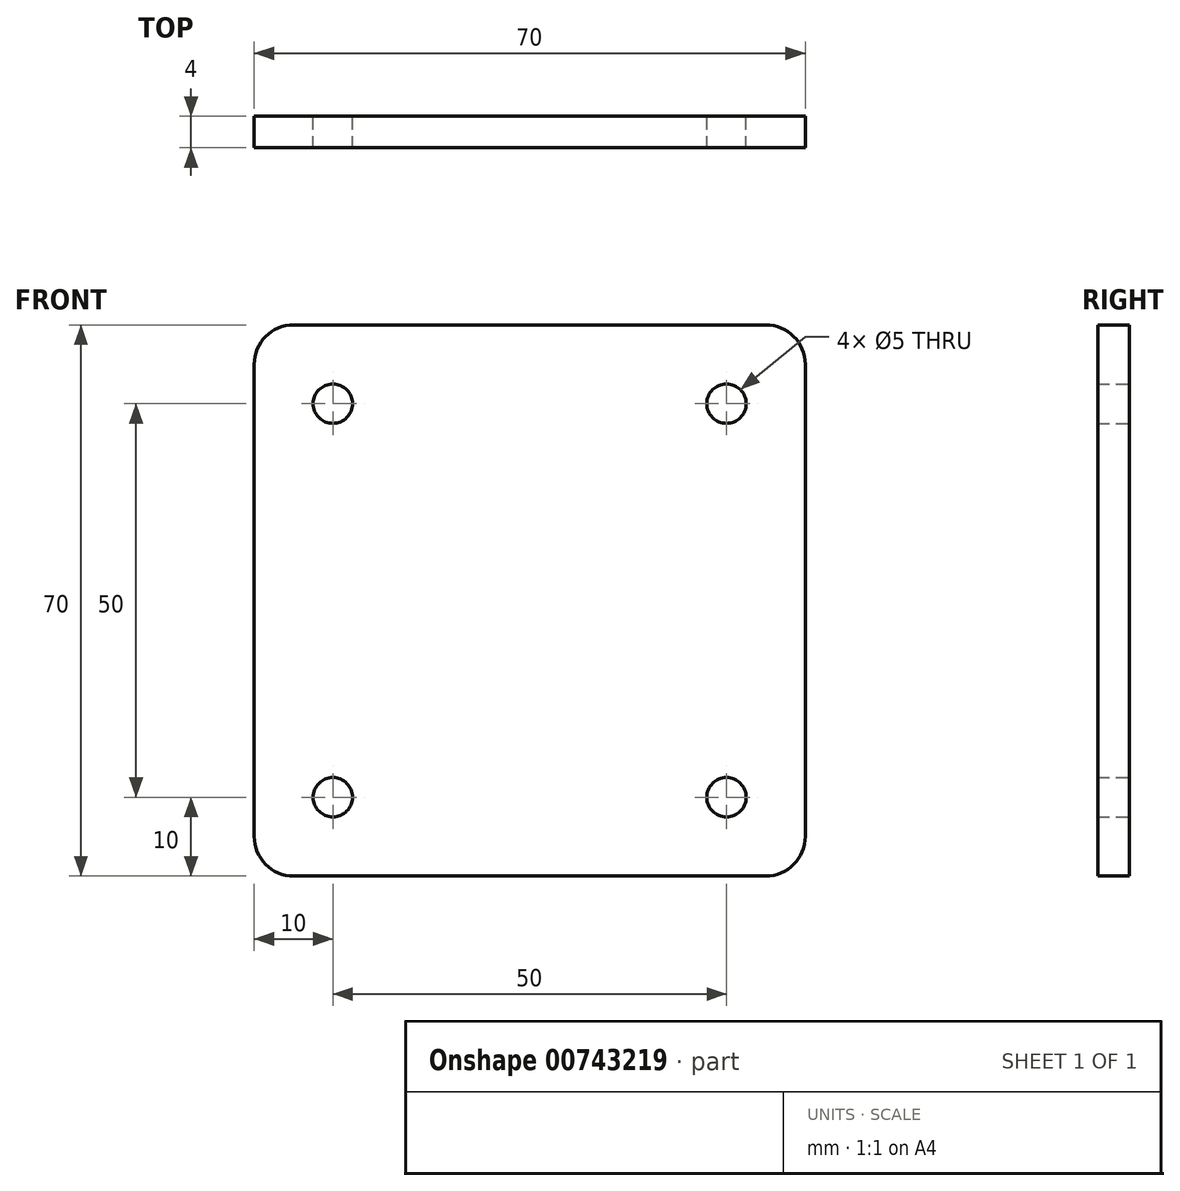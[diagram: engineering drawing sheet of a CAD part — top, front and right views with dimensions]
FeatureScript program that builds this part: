
annotation { "Feature Type Name" : "Feature", "Feature Type Description" : "" }
export const myFeature = defineFeature(function(context is Context, id is Id, definition is map)
    precondition{}
    {
        {
            var Q0;
            Q0=qCreatedBy(makeId("Front.planeOp"),FACE);
            var sketch = newSketch(context, id + "F0", { "sketchPlane" : qUnion([Q0])});
            skLineSegment(sketch, "E0.bottom", {"start": v(-30, 35) * mm, "end": v(30, 35) * mm});
            skLineSegment(sketch, "E0.top", {"start": v(-30, -35) * mm, "end": v(30, -35) * mm});
            skLineSegment(sketch, "E0.left", {"start": v(-35, 30) * mm, "end": v(-35, -30) * mm});
            skLineSegment(sketch, "E0.right", {"start": v(35, 30) * mm, "end": v(35, -30) * mm});
            skPoint(sketch, "E0.middle", {"position": v(0, 0) * mm});
            skLineSegment(sketch, "E1.bottom", {"start": v(-25, 25) * mm, "end": v(25, 25) * mm, "construction": true});
            skLineSegment(sketch, "E1.top", {"start": v(-25, -25) * mm, "end": v(25, -25) * mm, "construction": true});
            skLineSegment(sketch, "E1.left", {"start": v(-25, 25) * mm, "end": v(-25, -25) * mm, "construction": true});
            skLineSegment(sketch, "E1.right", {"start": v(25, 25) * mm, "end": v(25, -25) * mm, "construction": true});
            skCircle(sketch, "E2", {"center": v(-25, 25) * mm, "radius": 2.5 * mm});
            skCircle(sketch, "E3", {"center": v(25, 25) * mm, "radius": 2.5 * mm});
            skCircle(sketch, "E4", {"center": v(25, -25) * mm, "radius": 2.5 * mm});
            skCircle(sketch, "E5", {"center": v(-25, -25) * mm, "radius": 2.5 * mm});
            skPoint(sketch, "E6.visualSharp", {"position": v(-35, 35) * mm});
            skArc(sketch, "E6.filletArc", {"start": v(-30, 35) * mm, "mid": v(-33.54, 33.54) * mm, "end": v(-35, 30) * mm});
            skPoint(sketch, "E7.visualSharp", {"position": v(35, 35) * mm});
            skArc(sketch, "E7.filletArc", {"start": v(35, 30) * mm, "mid": v(33.54, 33.54) * mm, "end": v(30, 35) * mm});
            skPoint(sketch, "E8.visualSharp", {"position": v(35, -35) * mm});
            skArc(sketch, "E8.filletArc", {"start": v(30, -35) * mm, "mid": v(33.54, -33.54) * mm, "end": v(35, -30) * mm});
            skPoint(sketch, "E9.visualSharp", {"position": v(-35, -35) * mm});
            skArc(sketch, "E9.filletArc", {"start": v(-35, -30) * mm, "mid": v(-33.54, -33.54) * mm, "end": v(-30, -35) * mm});
            skSolve(sketch);
        }
        {
            var Q0;
            Q0=makeQuery(id+"F0.imprint","IMPRINT",FACE,{"disambiguationData":[TD([[makeQuery(id+"F0.imprint","IMPRINT",EDGE,{"derivedFrom":sQuery(id+"F0.wireOp",EDGE,"E0.bottom")}),-1.0]])]});
            extrude(context, id + "F1", {"entities" : qUnion([Q0]), "flatOperationType" : FlatOperationType.REMOVE, "depth" : 4 * mm, "offsetDistance" : 25 * mm, "domain" : OperationDomain.MODEL});
        }
    });
